FCSTD DOCUMENT  (FreeCAD 0.16R6706 (Git))
Label: tibia
License: All rights reserved
LicenseURL: http://en.wikipedia.org/wiki/All_rights_reserved
objects: Sketcher::SketchObject×1
note: 1 computed .brp shape members not serialized (recipe doc carries the construction recipe); baked Part::Feature solids carry a one-line shape summary decoded from their .brp

FEATURE [Sketcher::SketchObject] Sketch  label="tibia"
  sketch-geometry (24):
    g0: LineSegment StartX=-5.9 StartY=-2.9 StartZ=0 EndX=5.9 EndY=-2.9 EndZ=0
    g1: LineSegment StartX=5.9 StartY=-2.9 StartZ=0 EndX=5.9 EndY=-25.4 EndZ=0
    g2: LineSegment StartX=5.9 StartY=-25.4 StartZ=0 EndX=-5.9 EndY=-25.4 EndZ=0
    g3: LineSegment StartX=-5.9 StartY=-25.4 StartZ=0 EndX=-5.9 EndY=-2.9 EndZ=0
    g4: Circle CenterX=0 CenterY=-28.3 CenterZ=0 NormalX=0 NormalY=0 NormalZ=1 Radius=1.2
    g5: ArcOfCircle CenterX=0 CenterY=-7.9 CenterZ=0 NormalX=0 NormalY=0 NormalZ=1 Radius=12.2859 StartAngle=6.13809 EndAngle=9.40059
    g6: ArcOfCircle CenterX=127.677 CenterY=-10.9894 CenterZ=0 NormalX=0 NormalY=0 NormalZ=1 Radius=140 StartAngle=3.1174 EndAngle=3.84262
    g7: ArcOfCircle CenterX=175.423 CenterY=-33.5332 CenterZ=0 NormalX=0 NormalY=0 NormalZ=1 Radius=165 StartAngle=2.9965 EndAngle=3.55093
    g8: ArcOfCircle CenterX=22.22 CenterY=-100 CenterZ=0 NormalX=0 NormalY=0 NormalZ=1 Radius=2 StartAngle=3.84262 EndAngle=6.69253
    g9: LineSegment StartX=-5.56405 StartY=-32.6205 StartZ=0 EndX=5.10388 EndY=-30.8886 EndZ=0
    g10: ArcOfCircle CenterX=5.42437 CenterY=-32.8627 CenterZ=0 NormalX=0 NormalY=0 NormalZ=1 Radius=2 StartAngle=6.27924 EndAngle=8.01492
    g11: ArcOfCircle CenterX=-5.24356 CenterY=-34.5946 CenterZ=0 NormalX=0 NormalY=0 NormalZ=1 Radius=2 StartAngle=1.73174 EndAngle=3.31735
    g12: ArcOfCircle CenterX=175.423 CenterY=-33.5332 CenterZ=0 NormalX=0 NormalY=0 NormalZ=1 Radius=168 StartAngle=3.13765 EndAngle=3.23043
    g13: ArcOfCircle CenterX=127.677 CenterY=-10.9894 CenterZ=0 NormalX=0 NormalY=0 NormalZ=1 Radius=137 StartAngle=3.31735 EndAngle=3.44261
    g14: ArcOfCircle CenterX=6.09339 CenterY=-48.6152 CenterZ=0 NormalX=0 NormalY=0 NormalZ=1 Radius=2 StartAngle=5.02822 EndAngle=6.37202
    g15: ArcOfCircle CenterX=-1.25308 CenterY=-51.0158 CenterZ=0 NormalX=0 NormalY=0 NormalZ=1 Radius=2 StartAngle=3.44261 EndAngle=5.02822
    g16: LineSegment StartX=6.71461 StartY=-50.5163 StartZ=0 EndX=-0.631863 EndY=-52.9169 EndZ=0
    g17: LineSegment StartX=0.645879 StartY=-56.6421 StartZ=0 EndX=6.30393 EndY=-54.6087 EndZ=0
    g18: ArcOfCircle CenterX=6.98034 CenterY=-56.4909 CenterZ=0 NormalX=0 NormalY=0 NormalZ=1 Radius=2 StartAngle=0.135459 EndAngle=1.91581
    g19: ArcOfCircle CenterX=1.32229 CenterY=-58.5243 CenterZ=0 NormalX=0 NormalY=0 NormalZ=1 Radius=2 StartAngle=1.91581 EndAngle=3.50142
    g20: ArcOfCircle CenterX=127.677 CenterY=-10.9894 CenterZ=0 NormalX=0 NormalY=0 NormalZ=1 Radius=137 StartAngle=3.50142 EndAngle=3.73992
    g21: ArcOfCircle CenterX=175.423 CenterY=-33.5332 CenterZ=0 NormalX=0 NormalY=0 NormalZ=1 Radius=168 StartAngle=3.27705 EndAngle=3.46719
    g22: ArcOfCircle CenterX=15.3025 CenterY=-87.5925 CenterZ=0 NormalX=0 NormalY=0 NormalZ=1 Radius=1 StartAngle=3.73992 EndAngle=6.60879
    g23: Circle CenterX=0 CenterY=0 CenterZ=0 NormalX=0 NormalY=0 NormalZ=1 Radius=1.2
  constraints (79):
    c: Coincident(g0,g1)
    c: Coincident(g1,g2)
    c: Coincident(g2,g3)
    c: Coincident(g3,g0)
    c: Horizontal(g2)
    c: Vertical(g1)
    c: Vertical(g3)
    c: Distance(g0,g3) = 11.8
    c: Distance(g-1,g1) = 5.9
    c: Distance(g-1,g0) = 2.9
    c: Distance(g1,g0) = 22.5
    c: PointOnObject(g4,g-2)
    c: Radius(g4) = 1.2
    c: Distance(g4,g2) = 2.9
    c: Horizontal(g0)
    c: PointOnObject(g5,g-2)
    c: Distance(g5,g0) = 5
    c: Coincident(g5,g6)
    c: Tangent(g6,g5)
    c: Coincident(g8,g6)
    c: Tangent(g8,g6)
    c: Radius(g8) = 2
    c: Coincident(g7,g8)
    c: Tangent(g8,g7)
    c: DistanceY(g-1,g8) = -100
    c: Coincident(g5,g7)
    c: Tangent(g5,g7)
    c: PointOnObject(g6,g9)
    c: Coincident(g10,g9)
    c: Radius(g10) = 2
    c: Coincident(g11,g9)
    c: Radius(g11) = 2
    c: Tangent(g9,g10)
    c: Tangent(g11,g9)
    c: Coincident(g12,g7)
    c: Coincident(g12,g10)
    c: Coincident(g13,g6)
    c: Coincident(g13,g11)
    c: Tangent(g13,g11)
    c: Tangent(g12,g10)
    c: Coincident(g14,g12)
    c: Coincident(g15,g13)
    c: Radius(g15) = 2
    c: Radius(g14) = 2
    c: Tangent(g14,g12)
    c: Tangent(g15,g13)
    c: Coincident(g16,g14)
    c: PointOnObject(g6,g16)
    c: Tangent(g14,g16)
    c: Coincident(g15,g16)
    c: Tangent(g16,g15)
    c: Radius(g6) = 140
    c: Radius(g7) = 165
    c: DistanceX(g6) = 127.677
    c: DistanceY(g6) = -10.9894
    c: Radius(g13) = 137
    c: Radius(g12) = 168
    c: PointOnObject(g6,g17)
    c: Coincident(g18,g17)
    c: Radius(g18) = 2
    c: Tangent(g18,g17)
    c: Coincident(g19,g17)
    c: Radius(g19) = 2
    c: Tangent(g19,g17)
    c: Coincident(g20,g6)
    c: Coincident(g20,g19)
    c: Tangent(g20,g19)
    c: Coincident(g21,g7)
    c: Coincident(g21,g18)
    c: Tangent(g21,g18)
    c: Radius(g21) = 168
    c: Radius(g20) = 137
    c: Coincident(g22,g20)
    c: Coincident(g21,g22)
    c: Tangent(g20,g22)
    c: Tangent(g22,g21)
    c: Radius(g22) = 1
    c: Coincident(g23,g-1)
    c: Radius(g23) = 1.2
